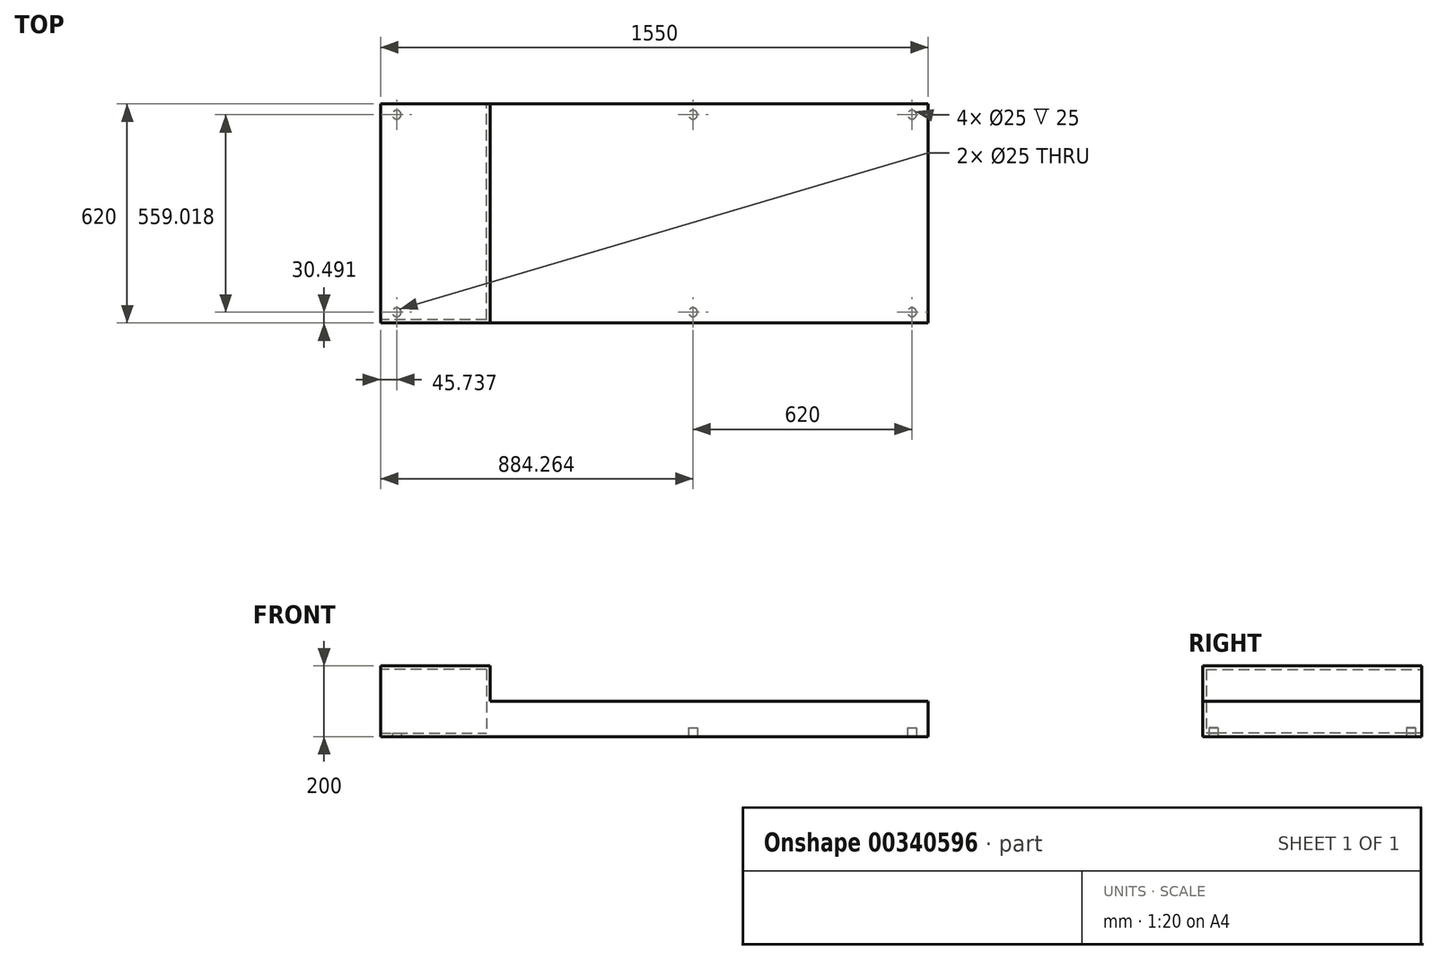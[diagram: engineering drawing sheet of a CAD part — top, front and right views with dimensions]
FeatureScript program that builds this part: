
annotation { "Feature Type Name" : "Feature", "Feature Type Description" : "" }
export const myFeature = defineFeature(function(context is Context, id is Id, definition is map)
    precondition{}
    {
        {
            var Q0;
            Q0=qCreatedBy(makeId("Front.planeOp"),FACE);
            var sketch = newSketch(context, id + "F0", { "sketchPlane" : qUnion([Q0])});
            skLineSegment(sketch, "E0.bottom", {"start": v(266.03, 63.05) * mm, "end": v(-353.97, 63.05) * mm});
            skLineSegment(sketch, "E0.top", {"start": v(266.03, -36.95) * mm, "end": v(-353.97, -36.95) * mm});
            skLineSegment(sketch, "E0.left", {"start": v(266.03, 63.05) * mm, "end": v(266.03, -36.95) * mm});
            skLineSegment(sketch, "E1", {"start": v(-353.97, 63.05) * mm, "end": v(-353.97, 163.05) * mm});
            skLineSegment(sketch, "E2", {"start": v(-353.97, 163.05) * mm, "end": v(-663.97, 163.05) * mm});
            skLineSegment(sketch, "E3", {"start": v(-663.97, 163.05) * mm, "end": v(-663.97, -36.95) * mm});
            skLineSegment(sketch, "E4", {"start": v(-663.97, -36.95) * mm, "end": v(-353.97, -36.95) * mm});
            skSolve(sketch);
        }
        {
            var Q0;
            Q0=qSketchRegion(id+"F0",true);
            extrude(context, id + "F1", {"entities" : qUnion([Q0]), "depth" : 620 * mm});
        }
        {
            var Q0;
            Q0=makeQuery(id+"F1.opExtrude","SWEPT_FACE",FACE,{"disambiguationData":[OSD([sQuery(id+"F0.wireOp",EDGE,"E0.top"),sQuery(id+"F0.wireOp",EDGE,"E4")])]});
            var sketch = newSketch(context, id + "F2", { "sketchPlane" : qUnion([Q0])});
            skCircle(sketch, "E5", {"center": v(-618.23, 589.5) * mm, "radius": 12.5 * mm});
            skCircle(sketch, "E6", {"center": v(-618.23, 30.5) * mm, "radius": 12.5 * mm});
            skCircle(sketch, "E7", {"center": v(220.3, 589.5) * mm, "radius": 12.5 * mm});
            skCircle(sketch, "E8", {"center": v(220.3, 30.5) * mm, "radius": 12.5 * mm});
            skSolve(sketch);
        }
        {
            var Q0;
            Q0=qSketchRegion(id+"F2",true);
            extrude(context, id + "F3", {"entities" : qUnion([Q0]), "operationType" : NewBodyOperationType.REMOVE, "oppositeDirection" : true, "depth" : 25 * mm});
        }
        {
            var Q0;
            Q0=makeQuery(id+"F1.opExtrude","SWEPT_FACE",FACE,{"disambiguationData":[OSD([sQuery(id+"F0.wireOp",EDGE,"E3")])]});
            var sketch = newSketch(context, id + "F4", { "sketchPlane" : qUnion([Q0])});
            skLineSegment(sketch, "E9.1", {"start": v(610, 153.05) * mm, "end": v(-39.18, 153.05) * mm});
            skLineSegment(sketch, "E9.3", {"start": v(-39.18, -26.95) * mm, "end": v(610, -26.95) * mm});
            skLineSegment(sketch, "E10", {"start": v(-39.18, 153.05) * mm, "end": v(-39.18, -26.95) * mm});
            skLineSegment(sketch, "E11", {"start": v(610, 153.05) * mm, "end": v(610, -26.95) * mm});
            skPoint(sketch, "E12.start.orphan", {"position": v(660.46, -26.95) * mm});
            skSolve(sketch);
        }
        {
            var Q0;
            Q0=qSketchRegion(id+"F4",true);
            extrude(context, id + "F5", {"entities" : qUnion([Q0]), "operationType" : NewBodyOperationType.REMOVE, "oppositeDirection" : true, "depth" : 300 * mm});
        }
        {
            var Q0;
            Q0=makeQuery(id+"F1.opExtrude","CAP_FACE",FACE,{"disambiguationData":[OSD([sQuery(id+"F0.wireOp",EDGE,"E0.bottom"),sQuery(id+"F0.wireOp",EDGE,"E0.top"),sQuery(id+"F0.wireOp",EDGE,"E0.left"),sQuery(id+"F0.wireOp",EDGE,"E1"),sQuery(id+"F0.wireOp",EDGE,"E2"),sQuery(id+"F0.wireOp",EDGE,"E3"),sQuery(id+"F0.wireOp",EDGE,"E4")])],"isStart":true});
            var sketch = newSketch(context, id + "F6", { "sketchPlane" : qUnion([Q0])});
            skLineSegment(sketch, "E13.bottom", {"start": v(-266.03, 63.05) * mm, "end": v(-886.03, 63.05) * mm});
            skLineSegment(sketch, "E13.top", {"start": v(-266.03, -36.95) * mm, "end": v(-886.03, -36.95) * mm});
            skLineSegment(sketch, "E13.left", {"start": v(-266.03, 63.05) * mm, "end": v(-266.03, -36.95) * mm});
            skLineSegment(sketch, "E13.right", {"start": v(-886.03, 63.05) * mm, "end": v(-886.03, -36.95) * mm});
            skSolve(sketch);
        }
        {
            var Q0;
            Q0=qSketchRegion(id+"F6",true);
            var Q1;
            Q1=makeQuery(id+"F1.opExtrude","CAP_FACE",FACE,{"disambiguationData":[OSD([sQuery(id+"F0.wireOp",EDGE,"E0.bottom"),sQuery(id+"F0.wireOp",EDGE,"E0.top"),sQuery(id+"F0.wireOp",EDGE,"E0.left"),sQuery(id+"F0.wireOp",EDGE,"E1"),sQuery(id+"F0.wireOp",EDGE,"E2"),sQuery(id+"F0.wireOp",EDGE,"E3"),sQuery(id+"F0.wireOp",EDGE,"E4")])],"isStart":false});
            extrude(context, id + "F7", {"entities" : qUnion([Q0]), "operationType" : NewBodyOperationType.ADD, "endBound" : BoundingType.UP_TO_SURFACE, "oppositeDirection" : true, "endBoundEntityFace" : qUnion([Q1]), "depth" : 25 * mm});
        }
        {
            var Q0;
            Q0=makeQuery(id+"F7.boolean.opBoolean","MERGE",FACE,{"derivedFrom":[makeQuery(id+"F1.opExtrude","SWEPT_FACE",FACE,{"disambiguationData":[OSD([sQuery(id+"F0.wireOp",EDGE,"E0.top"),sQuery(id+"F0.wireOp",EDGE,"E4")])]}),makeQuery(id+"F7.opExtrude","SWEPT_FACE",FACE,{"disambiguationData":[OSD([sQuery(id+"F6.wireOp",EDGE,"E13.top")])]})]});
            var sketch = newSketch(context, id + "F8", { "sketchPlane" : qUnion([Q0])});
            skCircle(sketch, "E14.MirrorC", {"center": v(840.3, 589.5) * mm, "radius": 12.5 * mm});
            skCircle(sketch, "E15.MirrorC", {"center": v(840.3, 30.5) * mm, "radius": 12.5 * mm});
            skPoint(sketch, "E16.start.orphan", {"position": v(111.03, 310) * mm});
            skPoint(sketch, "E17.orphan", {"position": v(886.03, 310) * mm});
            skPoint(sketch, "E18.start.orphan", {"position": v(-663.97, 310) * mm});
            skSolve(sketch);
        }
        {
            var Q0;
            Q0=qSketchRegion(id+"F8",true);
            var Q1;
            Q1=makeQuery(id+"F3.boolean.opBoolean","COPY",FACE,{"derivedFrom":makeQuery(id+"F3.opExtrude","CAP_FACE",FACE,{"disambiguationData":[OSD([sQuery(id+"F2.wireOp",EDGE,"E7")])],"isStart":false})});
            extrude(context, id + "F9", {"entities" : qUnion([Q0]), "operationType" : NewBodyOperationType.REMOVE, "endBound" : BoundingType.UP_TO_SURFACE, "oppositeDirection" : true, "endBoundEntityFace" : qUnion([Q1]), "depth" : 25 * mm});
        }
    });
